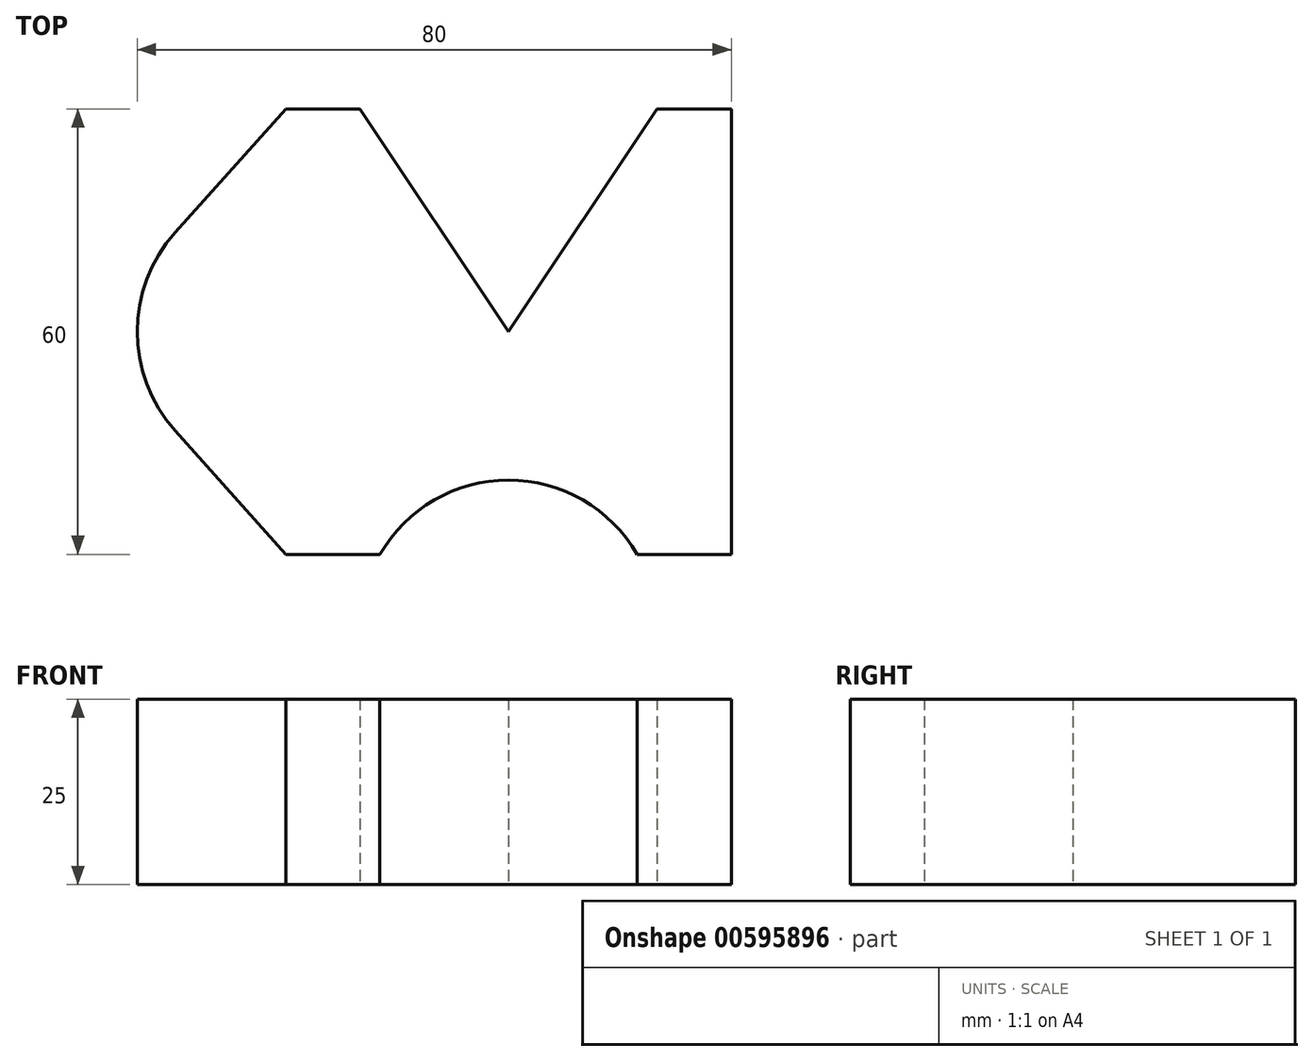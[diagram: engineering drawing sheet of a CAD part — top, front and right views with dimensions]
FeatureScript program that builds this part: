
annotation { "Feature Type Name" : "Feature", "Feature Type Description" : "" }
export const myFeature = defineFeature(function(context is Context, id is Id, definition is map)
    precondition{}
    {
        {
            var Q0;
            Q0=qCreatedBy(makeId("Top.planeOp"),FACE);
            var sketch = newSketch(context, id + "F0", { "sketchPlane" : qUnion([Q0])});
            skLineSegment(sketch, "E0", {"start": v(-20, 30) * mm, "end": v(0, 0) * mm});
            skLineSegment(sketch, "E1", {"start": v(0, 0) * mm, "end": v(20, 30) * mm});
            skLineSegment(sketch, "E2", {"start": v(20, 30) * mm, "end": v(30, 30) * mm});
            skLineSegment(sketch, "E3", {"start": v(30, 30) * mm, "end": v(30, -30) * mm});
            skLineSegment(sketch, "E4", {"start": v(30, -30) * mm, "end": v(17.32, -30) * mm});
            skArc(sketch, "E5", {"start": v(17.32, -30) * mm, "mid": v(0, -20) * mm, "end": v(-17.32, -30) * mm});
            skLineSegment(sketch, "E6", {"start": v(-17.32, -30) * mm, "end": v(-30, -30) * mm});
            skLineSegment(sketch, "E7", {"start": v(-30, -30) * mm, "end": v(-44.9, -13.33) * mm});
            skArc(sketch, "E8", {"start": v(-44.9, 13.33) * mm, "mid": v(-50, 0) * mm, "end": v(-44.9, -13.33) * mm});
            skLineSegment(sketch, "E9", {"start": v(-44.9, 13.33) * mm, "end": v(-30, 30) * mm});
            skLineSegment(sketch, "E10", {"start": v(-30, 30) * mm, "end": v(-20, 30) * mm});
            skLineSegment(sketch, "E11", {"start": v(-30, 30) * mm, "end": v(-30, -30) * mm, "construction": true});
            skSolve(sketch);
        }
        {
            var Q0;
            Q0=makeQuery(id+"F0.imprint","IMPRINT",FACE,{"disambiguationData":[TD([[makeQuery(id+"F0.imprint","IMPRINT",EDGE,{"derivedFrom":sQuery(id+"F0.wireOp",EDGE,"E0")}),-1.0]])]});
            extrude(context, id + "F1", {"entities" : qUnion([Q0]), "depth" : 25 * mm, "offsetDistance" : 25 * mm});
        }
    });
